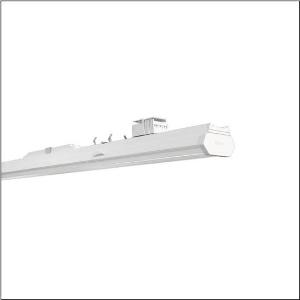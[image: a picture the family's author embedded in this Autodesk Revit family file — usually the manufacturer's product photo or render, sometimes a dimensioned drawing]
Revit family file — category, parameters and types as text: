
# Revit family: licross_r__11_protected_mo_51td127n485g_dbd9
name_source: partatom
category: Lighting Fixtures
units: mm (PartAtom-declared; Revit-internal decimal feet)

## family parameters
Cut with Voids When Loaded = No
Host = Face
Light Source = No
Part Type = Normal
Room Calculation Point = No
Round Connector Dimension = Use Diameter
Shared = No

## types (1)
- Licross® 11 Protected MO (1 x LED, 8720 lm, 48.6 W, 4000K)
    Apparent Load = 49 VA
    CIE Flux Codes = 73 92 98 99 100
    Color Rendering = 80
    Color Temperature = 4000K
    Default Elevation = 1800 mm
    Description = Licross® 11 Protected MO, luminaire insert, of sheet steel, galvanised, coil coated, white, length: 1.500mm, width: 90mm, height: 101mm, LED rated luminous flux: 8.720lm, light colour: 840, control gear: ON/OFF, with plug, 3-pole, with phase selection, mains connection: 220..240V, AC, 50/60Hz, rated input power: 49W, halogen-free wiring, primary light control with lens, of plastic, primary optical cover: cover, of PMMA, light emission: direct distribution, primary light characteristic: symmetric, protection rating (complete): IP54, insulation class (complete): insulation class I (protective earthing), certification: CE, ENEC, VDE, UKCA, protection symbol: D if used in an environment with non-conductive dust loads with corresponding accessories, impact resistance: IK06, permissible ambient temperature for indoor applications: -25..+35°C, corresponds to IFS (International Featured Standards) requirements for safety and quality in the food industry, reducing of maximum allowable ambient temperature of 5°C with ceiling mounting, LABS conformity tested according to VDMA 24364:2018-05, packaging unit: 1 piece
    Height = 92 mm
    Lamp = 1 x LED
    Lamp Light Flux = 8720 lm
    Lamp Power = 48.6 W
    Lamp count = 1
    Length = 1500 mm
    Luminous efficacy = 179 lm/W
    Manufacturer = Siteco
    ModVariant = No
    Model = 51TD127N485G
    Mounting Place = Ceiling
    Mounting Type = Pendant
    Number of Poles = 1
    OnlyDefault = Yes
    Power Factor = 1
    Product Name = Licross® 11 Protected MO
    Product group = luminaire insert
    ProductGroupID = 901
    Protection Class = Protection class I
    Protection Degree = IP 54
    RLX_Detail_Level = 1
    RLX_Emergency_Light_Flux = 0 lm
    RLX_Emergency_Type = 0
    RLX_Emergency_Type_DB = No
    RlxData = <blob elided: 20653 chars, md5=cdf4117f>
    Socket = socket
    Standby Power = 0 W
    System Light Flux = 8720 lm
    System Power = 49 W
    Type Comments = Product without accessories
    Type Image = l_1256145.jpg
    URL = http://relux.com
    VarID = ---
    Voltage = 0 V
    Weight = 0.00 kg
    Width = 88 mm

## geometry (parser evidence)
native form markers: Blend x4, Sweep x11
no freeform markers — native parametric forms only
